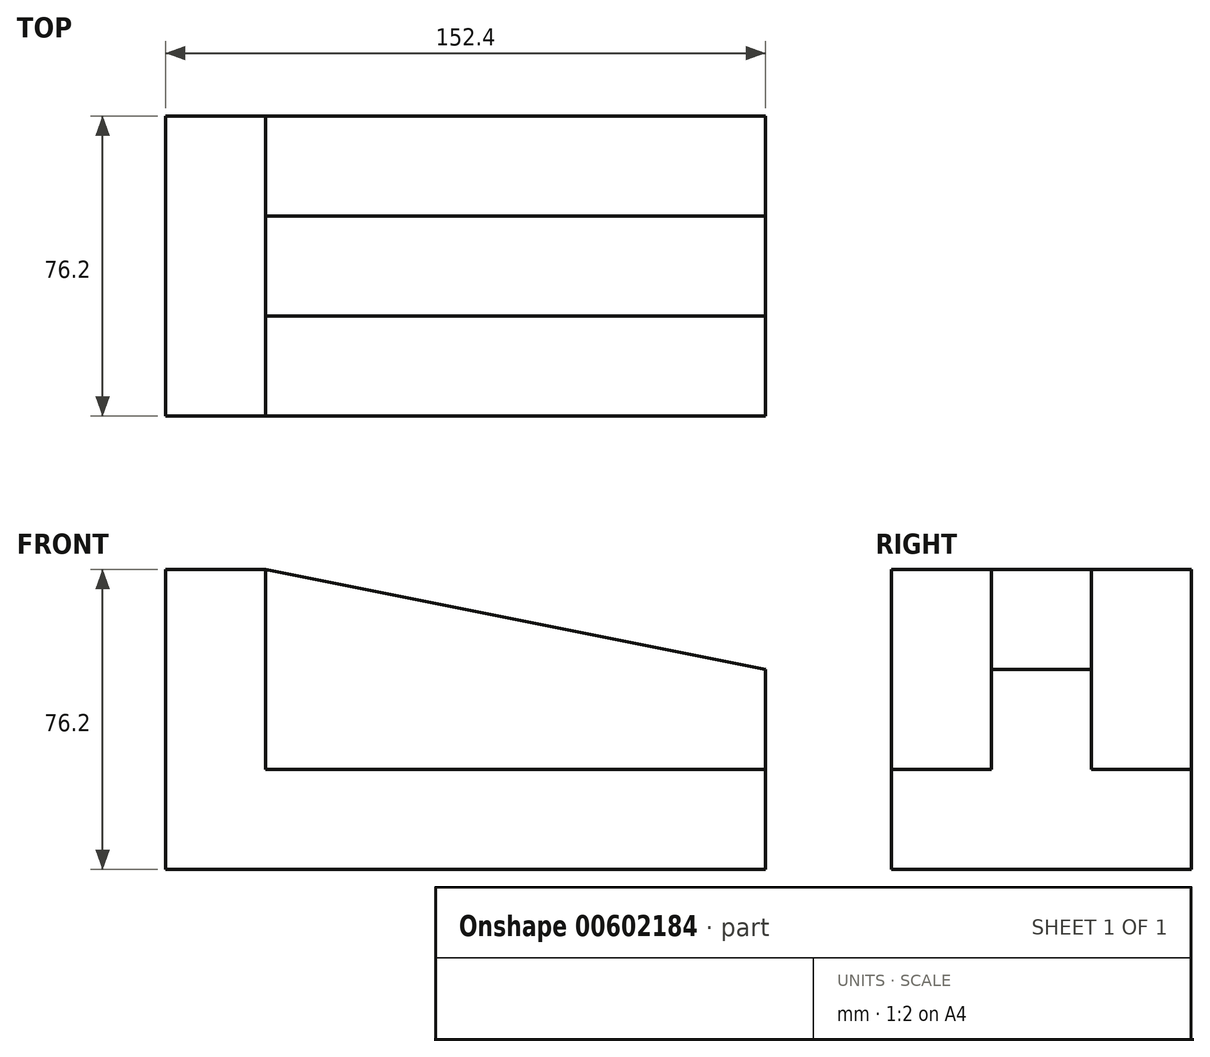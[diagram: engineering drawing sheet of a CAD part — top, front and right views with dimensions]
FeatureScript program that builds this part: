
annotation { "Feature Type Name" : "Feature", "Feature Type Description" : "" }
export const myFeature = defineFeature(function(context is Context, id is Id, definition is map)
    precondition{}
    {
        {
            var Q0;
            Q0=qCreatedBy(makeId("Front.planeOp"),FACE);
            var sketch = newSketch(context, id + "F0", { "sketchPlane" : qUnion([Q0])});
            skLineSegment(sketch, "E0", {"start": v(16.1, 0) * mm, "end": v(168.5, 0) * mm});
            skLineSegment(sketch, "E1", {"start": v(168.5, 0) * mm, "end": v(168.5, 50.8) * mm});
            skLineSegment(sketch, "E2", {"start": v(168.5, 50.8) * mm, "end": v(16.1, 50.8) * mm});
            skLineSegment(sketch, "E3", {"start": v(16.1, 50.8) * mm, "end": v(16.1, 0) * mm});
            skSolve(sketch);
        }
        {
            var Q0;
            Q0=makeQuery(id+"F0.imprint","IMPRINT",FACE,{"disambiguationData":[TD([[makeQuery(id+"F0.imprint","IMPRINT",EDGE,{"derivedFrom":sQuery(id+"F0.wireOp",EDGE,"E0")}),1.0]])]});
            extrude(context, id + "F1", {"entities" : qUnion([Q0]), "depth" : 76.2 * mm, "offsetDistance" : 25.4 * mm});
        }
        {
            var Q0;
            Q0=makeQuery(id+"F1.opExtrude","SWEPT_FACE",FACE,{"disambiguationData":[OSD([sQuery(id+"F0.wireOp",EDGE,"E2")])]});
            var sketch = newSketch(context, id + "F2", { "sketchPlane" : qUnion([Q0])});
            skLineSegment(sketch, "E4", {"start": v(41.5, -76.2) * mm, "end": v(41.5, 0) * mm});
            skLineSegment(sketch, "E5", {"start": v(41.5, 0) * mm, "end": v(16.1, 0) * mm});
            skLineSegment(sketch, "E6", {"start": v(16.1, 0) * mm, "end": v(16.1, -76.2) * mm});
            skLineSegment(sketch, "E7", {"start": v(16.1, -76.2) * mm, "end": v(41.5, -76.2) * mm});
            skSolve(sketch);
        }
        {
            var Q0;
            Q0=makeQuery(id+"F2.imprint","IMPRINT",FACE,{"disambiguationData":[TD([[makeQuery(id+"F2.imprint","IMPRINT",EDGE,{"derivedFrom":sQuery(id+"F2.wireOp",EDGE,"E4")}),1.0]])]});
            extrude(context, id + "F3", {"entities" : qUnion([Q0]), "operationType" : NewBodyOperationType.ADD, "depth" : 25.4 * mm, "offsetDistance" : 25.4 * mm});
        }
        {
            var Q0;
            Q0=makeQuery(id+"F1.opExtrude","SWEPT_FACE",FACE,{"disambiguationData":[OSD([sQuery(id+"F0.wireOp",EDGE,"E2")])]});
            var sketch = newSketch(context, id + "F4", { "sketchPlane" : qUnion([Q0])});
            skLineSegment(sketch, "E8", {"start": v(41.5, -25.4) * mm, "end": v(168.5, -25.4) * mm});
            skLineSegment(sketch, "E9", {"start": v(41.5, -50.8) * mm, "end": v(168.5, -50.8) * mm});
            skLineSegment(sketch, "E10", {"start": v(41.5, -25.4) * mm, "end": v(41.5, 0) * mm});
            skLineSegment(sketch, "E11", {"start": v(41.5, -50.8) * mm, "end": v(41.5, -76.2) * mm});
            skLineSegment(sketch, "E12", {"start": v(41.5, -25.4) * mm, "end": v(41.5, -50.8) * mm});
            skSolve(sketch);
        }
        {
            var Q0;
            {var subQ0=sQuery(id+"F4.wireOp",EDGE,"E8");Q0=makeQuery(id+"F4.imprint","IMPRINT",FACE,{"disambiguationData":[TD([[makeQuery(id+"F4.imprint","IMPRINT",EDGE,{"derivedFrom":subQ0}),-1.0]])]});}
            extrude(context, id + "F5", {"entities" : qUnion([Q0]), "operationType" : NewBodyOperationType.ADD, "depth" : 25.4 * mm, "offsetDistance" : 25.4 * mm});
        }
        {
            var Q0;
            Q0=makeQuery(id+"F5.opExtrude","SWEPT_FACE",FACE,{"disambiguationData":[OSD([sQuery(id+"F4.wireOp",EDGE,"E9")])]});
            var sketch = newSketch(context, id + "F6", { "sketchPlane" : qUnion([Q0])});
            skLineSegment(sketch, "E13", {"start": v(168.5, 50.8) * mm, "end": v(41.5, 76.2) * mm});
            skLineSegment(sketch, "E14", {"start": v(41.5, 76.2) * mm, "end": v(168.5, 76.2) * mm});
            skLineSegment(sketch, "E15", {"start": v(168.5, 76.2) * mm, "end": v(168.5, 50.8) * mm});
            skSolve(sketch);
        }
        {
            var Q0;
            Q0=makeQuery(id+"F6.imprint","IMPRINT",FACE,{"disambiguationData":[TD([[makeQuery(id+"F6.imprint","IMPRINT",EDGE,{"derivedFrom":sQuery(id+"F6.wireOp",EDGE,"E13")}),-1.0]])]});
            extrude(context, id + "F7", {"entities" : qUnion([Q0]), "operationType" : NewBodyOperationType.REMOVE, "oppositeDirection" : true, "depth" : 25.4 * mm, "offsetDistance" : 25.4 * mm});
        }
        {
            var Q0;
            {var subQ1=sQuery(id+"F0.wireOp",EDGE,"E2");Q0=makeQuery(id+"F5.boolean.opBoolean","SPLIT",FACE,{"disambiguationData":[TD([makeQuery(id+"F3.opExtrude","SWEPT_FACE",FACE,{"disambiguationData":[OSD([sQuery(id+"F2.wireOp",EDGE,"E7")])]})])],"derivedFrom":makeQuery(id+"F1.opExtrude","SWEPT_FACE",FACE,{"disambiguationData":[OSD([subQ1])]})});}
            extrude(context, id + "F8", {"entities" : qUnion([Q0]), "operationType" : NewBodyOperationType.REMOVE, "oppositeDirection" : true, "depth" : 25.4 * mm, "offsetDistance" : 25.4 * mm});
        }
        {
            var Q0;
            {var subQ0=sQuery(id+"F0.wireOp",EDGE,"E2");Q0=makeQuery(id+"F5.boolean.opBoolean","SPLIT",FACE,{"disambiguationData":[TD([makeQuery(id+"F3.opExtrude","SWEPT_FACE",FACE,{"disambiguationData":[OSD([sQuery(id+"F2.wireOp",EDGE,"E5")])]})])],"derivedFrom":makeQuery(id+"F1.opExtrude","SWEPT_FACE",FACE,{"disambiguationData":[OSD([subQ0])]})});}
            extrude(context, id + "F9", {"entities" : qUnion([Q0]), "operationType" : NewBodyOperationType.REMOVE, "oppositeDirection" : true, "depth" : 25.4 * mm, "offsetDistance" : 25.4 * mm});
        }
    });
